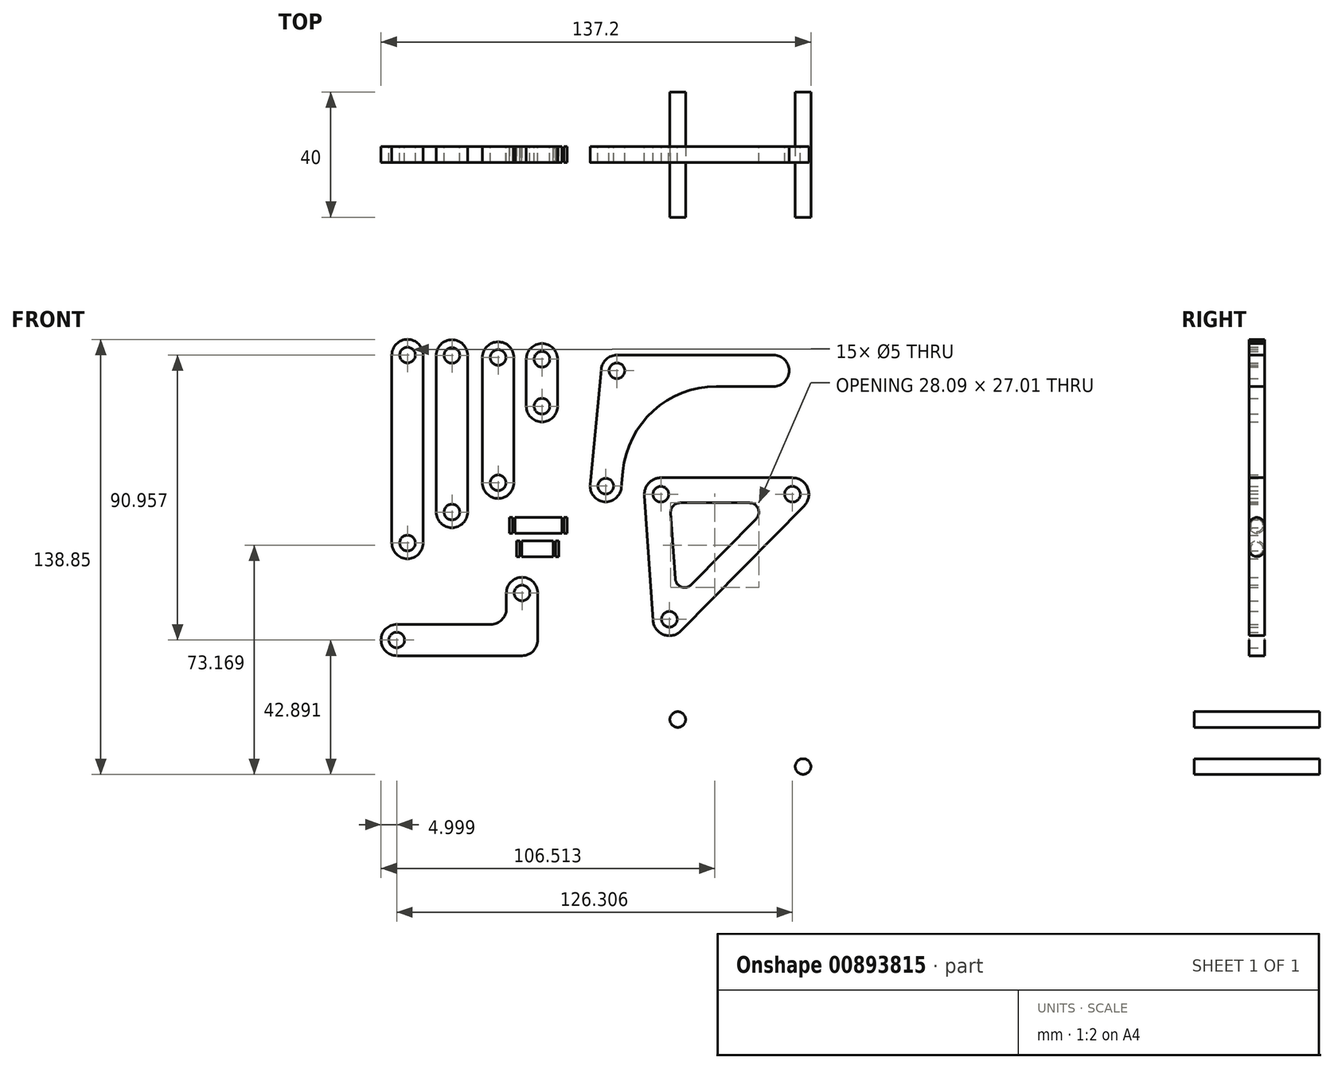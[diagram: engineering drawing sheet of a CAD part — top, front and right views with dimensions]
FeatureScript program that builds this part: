
annotation { "Feature Type Name" : "Feature", "Feature Type Description" : "" }
export const myFeature = defineFeature(function(context is Context, id is Id, definition is map)
    precondition{}
    {
        {
            assignVariable(context, id + "F0", {"name" : "T", "anyValue" : 5});
        }
        {
            assignVariable(context, id + "F1", {"name" : "W", "anyValue" : 40});
        }
        {
            var Q0;
            Q0=qCreatedBy(makeId("Front.planeOp"),FACE);
            var sketch = newSketch(context, id + "F2", { "sketchPlane" : qUnion([Q0])});
            skLineSegment(sketch, "E0", {"start": v(-8.35, 51.22) * mm, "end": v(-8.35, 66.22) * mm});
            skLineSegment(sketch, "E1", {"start": v(-18.35, 51.22) * mm, "end": v(-18.35, 66.22) * mm});
            skArc(sketch, "E2", {"start": v(-8.35, 66.22) * mm, "mid": v(-13.35, 71.22) * mm, "end": v(-18.35, 66.22) * mm});
            skArc(sketch, "E3", {"start": v(-18.35, 51.22) * mm, "mid": v(-13.35, 46.22) * mm, "end": v(-8.35, 51.22) * mm});
            skCircle(sketch, "E4", {"center": v(-13.35, 66.22) * mm, "radius": 2.5 * mm});
            skCircle(sketch, "E5", {"center": v(-13.35, 51.22) * mm, "radius": 2.5 * mm});
            skSolve(sketch);
        }
        {
            var Q0;
            Q0=qSketchRegion(id+"F2",true);
            extrude(context, id + "F3", {"entities" : qUnion([Q0]), "depth" : (getVariable(context, 'T')) * mm, "offsetDistance" : 25 * mm, "symmetric" : true});
        }
        {
            var Q0;
            Q0=qCreatedBy(makeId("Front.planeOp"),FACE);
            var sketch = newSketch(context, id + "F4", { "sketchPlane" : qUnion([Q0])});
            skLineSegment(sketch, "E6", {"start": v(-32.34, 66.78) * mm, "end": v(-32.34, 26.78) * mm});
            skLineSegment(sketch, "E7", {"start": v(-22.34, 26.78) * mm, "end": v(-22.34, 66.78) * mm});
            skArc(sketch, "E8", {"start": v(-22.34, 66.78) * mm, "mid": v(-27.34, 71.78) * mm, "end": v(-32.34, 66.78) * mm});
            skArc(sketch, "E9", {"start": v(-32.34, 26.78) * mm, "mid": v(-27.34, 21.78) * mm, "end": v(-22.34, 26.78) * mm});
            skCircle(sketch, "E10", {"center": v(-27.34, 26.78) * mm, "radius": 2.5 * mm});
            skCircle(sketch, "E11", {"center": v(-27.34, 66.78) * mm, "radius": 2.5 * mm});
            skSolve(sketch);
        }
        {
            var Q0;
            Q0=qSketchRegion(id+"F4",true);
            extrude(context, id + "F5", {"entities" : qUnion([Q0]), "depth" : (getVariable(context, 'T')) * mm, "offsetDistance" : 25 * mm, "symmetric" : true});
        }
        {
            var Q0;
            Q0=qCreatedBy(makeId("Front.planeOp"),FACE);
            var sketch = newSketch(context, id + "F6", { "sketchPlane" : qUnion([Q0])});
            skLineSegment(sketch, "E12", {"start": v(-47.08, 67.45) * mm, "end": v(-47.08, 17.45) * mm});
            skLineSegment(sketch, "E13", {"start": v(-37.08, 67.45) * mm, "end": v(-37.08, 17.45) * mm});
            skArc(sketch, "E14", {"start": v(-47.08, 17.45) * mm, "mid": v(-42.08, 12.45) * mm, "end": v(-37.08, 17.45) * mm});
            skArc(sketch, "E15", {"start": v(-37.08, 67.45) * mm, "mid": v(-42.08, 72.45) * mm, "end": v(-47.08, 67.45) * mm});
            skCircle(sketch, "E16", {"center": v(-42.08, 67.45) * mm, "radius": 2.5 * mm});
            skCircle(sketch, "E17", {"center": v(-42.08, 17.45) * mm, "radius": 2.5 * mm});
            skSolve(sketch);
        }
        {
            var Q0;
            Q0=qSketchRegion(id+"F6",true);
            extrude(context, id + "F7", {"entities" : qUnion([Q0]), "depth" : (getVariable(context, 'T')) * mm, "offsetDistance" : 25 * mm, "symmetric" : true});
        }
        {
            var Q0;
            Q0=qCreatedBy(makeId("Front.planeOp"),FACE);
            var sketch = newSketch(context, id + "F8", { "sketchPlane" : qUnion([Q0])});
            skLineSegment(sketch, "E18", {"start": v(-61.26, 67.56) * mm, "end": v(-61.26, 7.56) * mm});
            skLineSegment(sketch, "E19", {"start": v(-51.26, 7.56) * mm, "end": v(-51.26, 67.56) * mm});
            skArc(sketch, "E20", {"start": v(-51.26, 67.56) * mm, "mid": v(-56.26, 72.56) * mm, "end": v(-61.26, 67.56) * mm});
            skArc(sketch, "E21", {"start": v(-61.26, 7.56) * mm, "mid": v(-56.26, 2.56) * mm, "end": v(-51.26, 7.56) * mm});
            skCircle(sketch, "E22", {"center": v(-56.26, 67.56) * mm, "radius": 2.5 * mm});
            skCircle(sketch, "E23", {"center": v(-56.26, 7.56) * mm, "radius": 2.5 * mm});
            skSolve(sketch);
        }
        {
            var Q0;
            Q0=qSketchRegion(id+"F8",true);
            extrude(context, id + "F9", {"entities" : qUnion([Q0]), "depth" : (getVariable(context, 'T')) * mm, "offsetDistance" : 25 * mm, "symmetric" : true});
        }
        {
            var Q0;
            Q0=qCreatedBy(makeId("Front.planeOp"),FACE);
            var sketch = newSketch(context, id + "F10", { "sketchPlane" : qUnion([Q0])});
            skLineSegment(sketch, "E24", {"start": v(60.57, 67.55) * mm, "end": v(10.57, 67.55) * mm});
            skLineSegment(sketch, "E25", {"start": v(5.6, 63.03) * mm, "end": v(2.04, 26.2) * mm});
            skLineSegment(sketch, "E26", {"start": v(12, 25.24) * mm, "end": v(12.5, 30.44) * mm});
            skLineSegment(sketch, "E27", {"start": v(42.35, 57.55) * mm, "end": v(60.57, 57.55) * mm});
            skArc(sketch, "E28", {"start": v(2.04, 26.2) * mm, "mid": v(6.53, 20.74) * mm, "end": v(12, 25.24) * mm});
            skArc(sketch, "E29", {"start": v(10.57, 67.55) * mm, "mid": v(7.21, 66.25) * mm, "end": v(5.6, 63.03) * mm});
            skArc(sketch, "E30", {"start": v(60.57, 57.55) * mm, "mid": v(65.57, 62.55) * mm, "end": v(60.57, 67.55) * mm});
            skArc(sketch, "E31", {"start": v(42.35, 57.55) * mm, "mid": v(22.19, 49.76) * mm, "end": v(12.5, 30.44) * mm});
            skCircle(sketch, "E32", {"center": v(7.01, 25.72) * mm, "radius": 2.5 * mm});
            skCircle(sketch, "E33", {"center": v(10.57, 62.55) * mm, "radius": 2.5 * mm});
            skSolve(sketch);
        }
        {
            var Q0;
            Q0=makeQuery(id+"F10.imprint","IMPRINT",FACE,{"disambiguationData":[TD([[makeQuery(id+"F10.imprint","IMPRINT",EDGE,{"derivedFrom":sQuery(id+"F10.wireOp",EDGE,"E24")}),1.0]])]});
            extrude(context, id + "F11", {"entities" : qUnion([Q0]), "depth" : (getVariable(context, 'T')) * mm, "offsetDistance" : 25 * mm, "symmetric" : true});
        }
        {
            var Q0;
            Q0=qCreatedBy(makeId("Front.planeOp"),FACE);
            var sketch = newSketch(context, id + "F12", { "sketchPlane" : qUnion([Q0])});
            skLineSegment(sketch, "E34", {"start": v(19.37, 22.78) * mm, "end": v(22.08, -17.13) * mm});
            skLineSegment(sketch, "E35", {"start": v(31.06, -20.46) * mm, "end": v(70.35, 19.45) * mm});
            skLineSegment(sketch, "E36", {"start": v(66.6, 28.38) * mm, "end": v(24.6, 28.38) * mm});
            skArc(sketch, "E37", {"start": v(24.6, 28.38) * mm, "mid": v(20.77, 26.72) * mm, "end": v(19.37, 22.78) * mm});
            skArc(sketch, "E38", {"start": v(22.08, -17.13) * mm, "mid": v(25.5, -21.7) * mm, "end": v(31.06, -20.46) * mm});
            skArc(sketch, "E39", {"start": v(70.35, 19.45) * mm, "mid": v(71.45, 25.16) * mm, "end": v(66.6, 28.38) * mm});
            skCircle(sketch, "E40", {"center": v(24.6, 23.13) * mm, "radius": 2.5 * mm});
            skCircle(sketch, "E41", {"center": v(27.32, -16.77) * mm, "radius": 2.5 * mm});
            skCircle(sketch, "E42", {"center": v(66.6, 23.13) * mm, "radius": 2.5 * mm});
            skLineSegment(sketch, "E43", {"start": v(30.76, 20.38) * mm, "end": v(52.88, 20.38) * mm});
            skLineSegment(sketch, "E44", {"start": v(55.01, 15.28) * mm, "end": v(34.33, -5.74) * mm});
            skLineSegment(sketch, "E45", {"start": v(27.77, 17.18) * mm, "end": v(29.2, -3.83) * mm});
            skArc(sketch, "E46", {"start": v(29.2, -3.83) * mm, "mid": v(31.15, -6.44) * mm, "end": v(34.33, -5.74) * mm});
            skArc(sketch, "E47", {"start": v(30.76, 20.38) * mm, "mid": v(28.57, 19.43) * mm, "end": v(27.77, 17.18) * mm});
            skArc(sketch, "E48", {"start": v(55.01, 15.28) * mm, "mid": v(55.64, 18.54) * mm, "end": v(52.88, 20.38) * mm});
            skLineSegment(sketch, "E49", {"start": v(52.88, 28.38) * mm, "end": v(52.88, 20.38) * mm, "construction": true});
            skLineSegment(sketch, "E50", {"start": v(60.71, 9.67) * mm, "end": v(55.01, 15.28) * mm, "construction": true});
            skLineSegment(sketch, "E51", {"start": v(19.78, 16.64) * mm, "end": v(27.77, 17.18) * mm, "construction": true});
            skSolve(sketch);
        }
        {
            var Q0;
            Q0=qSketchRegion(id+"F12",true);
            extrude(context, id + "F13", {"entities" : qUnion([Q0]), "depth" : (getVariable(context, 'T')) * mm, "offsetDistance" : 25 * mm, "symmetric" : true});
        }
        {
            var Q0;
            Q0=qCreatedBy(makeId("Front.planeOp"),FACE);
            var sketch = newSketch(context, id + "F14", { "sketchPlane" : qUnion([Q0])});
            skLineSegment(sketch, "E52", {"start": v(-21.44, 5.72) * mm, "end": v(-21.44, 8.22) * mm});
            skLineSegment(sketch, "E53", {"start": v(-21.44, 8.22) * mm, "end": v(-20.44, 8.22) * mm});
            skLineSegment(sketch, "E54", {"start": v(-20.44, 8.22) * mm, "end": v(-20.44, 7.72) * mm});
            skLineSegment(sketch, "E55", {"start": v(-20.44, 7.72) * mm, "end": v(-19.74, 7.72) * mm});
            skLineSegment(sketch, "E56", {"start": v(-19.74, 7.72) * mm, "end": v(-19.74, 8.22) * mm});
            skLineSegment(sketch, "E57", {"start": v(-19.74, 8.22) * mm, "end": v(-9.74, 8.22) * mm});
            skLineSegment(sketch, "E58", {"start": v(-9.74, 8.22) * mm, "end": v(-9.74, 7.72) * mm});
            skLineSegment(sketch, "E59", {"start": v(-9.74, 7.72) * mm, "end": v(-9.04, 7.72) * mm});
            skLineSegment(sketch, "E60", {"start": v(-9.04, 7.72) * mm, "end": v(-9.04, 8.22) * mm});
            skLineSegment(sketch, "E61", {"start": v(-9.04, 8.22) * mm, "end": v(-8.04, 8.22) * mm});
            skLineSegment(sketch, "E62", {"start": v(-8.04, 8.22) * mm, "end": v(-8.04, 5.72) * mm});
            skLineSegment(sketch, "E63", {"start": v(-8.04, 5.72) * mm, "end": v(-21.44, 5.72) * mm});
            skSolve(sketch);
        }
        {
            var Q0;
            Q0=makeQuery(id+"F14.imprint","IMPRINT",FACE,{"disambiguationData":[TD([[makeQuery(id+"F14.imprint","IMPRINT",EDGE,{"derivedFrom":sQuery(id+"F14.wireOp",EDGE,"E52")}),-1.0]])]});
            var Q1;
            Q1=sQuery(id+"F14.wireOp",EDGE,"E63");
            revolve(context, id + "F15", {"surfaceOperationType" : NewSurfaceOperationType.NEW, "entities" : qUnion([Q0]), "axis" : qUnion([Q1]), "revolveType" : RevolveType.FULL});
        }
        {
            var Q0;
            Q0=qCreatedBy(makeId("Front.planeOp"),FACE);
            var sketch = newSketch(context, id + "F16", { "sketchPlane" : qUnion([Q0])});
            skLineSegment(sketch, "E64", {"start": v(-23.7, 15.7) * mm, "end": v(-23.7, 13.2) * mm});
            skLineSegment(sketch, "E65", {"start": v(-23.7, 13.2) * mm, "end": v(-5.3, 13.2) * mm});
            skLineSegment(sketch, "E66", {"start": v(-5.3, 13.2) * mm, "end": v(-5.3, 15.7) * mm});
            skLineSegment(sketch, "E67", {"start": v(-5.3, 15.7) * mm, "end": v(-6.3, 15.7) * mm});
            skLineSegment(sketch, "E68", {"start": v(-6.3, 15.7) * mm, "end": v(-6.3, 15.2) * mm});
            skLineSegment(sketch, "E69", {"start": v(-6.3, 15.2) * mm, "end": v(-7, 15.2) * mm});
            skLineSegment(sketch, "E70", {"start": v(-7, 15.2) * mm, "end": v(-7, 15.7) * mm});
            skLineSegment(sketch, "E71", {"start": v(-7, 15.7) * mm, "end": v(-22, 15.7) * mm});
            skLineSegment(sketch, "E72", {"start": v(-22, 15.7) * mm, "end": v(-22, 15.2) * mm});
            skLineSegment(sketch, "E73", {"start": v(-22, 15.2) * mm, "end": v(-22.7, 15.2) * mm});
            skLineSegment(sketch, "E74", {"start": v(-22.7, 15.2) * mm, "end": v(-22.7, 15.7) * mm});
            skLineSegment(sketch, "E75", {"start": v(-22.7, 15.7) * mm, "end": v(-23.7, 15.7) * mm});
            skSolve(sketch);
        }
        {
            var Q0;
            Q0=qSketchRegion(id+"F16",true);
            var Q1;
            Q1=sQuery(id+"F16.wireOp",EDGE,"E65");
            revolve(context, id + "F17", {"surfaceOperationType" : NewSurfaceOperationType.NEW, "entities" : qUnion([Q0]), "axis" : qUnion([Q1]), "revolveType" : RevolveType.FULL});
        }
        {
            var Q0;
            Q0=qCreatedBy(makeId("Front.planeOp"),FACE);
            var sketch = newSketch(context, id + "F18", { "sketchPlane" : qUnion([Q0])});
            skLineSegment(sketch, "E76", {"start": v(-59.7, -18.4) * mm, "end": v(-29.7, -18.4) * mm});
            skLineSegment(sketch, "E77", {"start": v(-24.7, -13.4) * mm, "end": v(-24.7, -8.4) * mm});
            skLineSegment(sketch, "E78", {"start": v(-14.7, -8.4) * mm, "end": v(-14.7, -23.4) * mm});
            skLineSegment(sketch, "E79", {"start": v(-19.7, -28.4) * mm, "end": v(-59.7, -28.4) * mm});
            skArc(sketch, "E80", {"start": v(-59.7, -18.4) * mm, "mid": v(-64.7, -23.4) * mm, "end": v(-59.7, -28.4) * mm});
            skArc(sketch, "E81", {"start": v(-14.7, -8.4) * mm, "mid": v(-19.7, -3.4) * mm, "end": v(-24.7, -8.4) * mm});
            skPoint(sketch, "E82.visualSharp", {"position": v(-24.7, -18.4) * mm});
            skArc(sketch, "E82.filletArc", {"start": v(-29.7, -18.4) * mm, "mid": v(-26.17, -16.93) * mm, "end": v(-24.7, -13.4) * mm});
            skPoint(sketch, "E83.visualSharp", {"position": v(-14.7, -28.4) * mm});
            skArc(sketch, "E83.filletArc", {"start": v(-19.7, -28.4) * mm, "mid": v(-16.17, -26.93) * mm, "end": v(-14.7, -23.4) * mm});
            skCircle(sketch, "E84", {"center": v(-59.7, -23.4) * mm, "radius": 2.5 * mm});
            skCircle(sketch, "E85", {"center": v(-19.7, -8.4) * mm, "radius": 2.5 * mm});
            skSolve(sketch);
        }
        {
            var Q0;
            Q0=qSketchRegion(id+"F18",true);
            extrude(context, id + "F19", {"entities" : qUnion([Q0]), "depth" : (getVariable(context, 'T')) * mm, "offsetDistance" : 25 * mm, "symmetric" : true});
        }
        {
            var Q0;
            Q0=qCreatedBy(makeId("Front.planeOp"),FACE);
            var sketch = newSketch(context, id + "F20", { "sketchPlane" : qUnion([Q0])});
            skLineSegment(sketch, "E86.bottom", {"start": v(-80, -39.79) * mm, "end": v(120, -39.79) * mm});
            skLineSegment(sketch, "E86.top", {"start": v(-80, -69.79) * mm, "end": v(120, -69.79) * mm});
            skLineSegment(sketch, "E86.left", {"start": v(-80, -39.79) * mm, "end": v(-80, -69.79) * mm});
            skLineSegment(sketch, "E86.right", {"start": v(120, -39.79) * mm, "end": v(120, -69.79) * mm});
            skSolve(sketch);
        }
        {
            var Q0;
            Q0=makeQuery(id+"F20.imprint","IMPRINT",FACE,{"disambiguationData":[TD([[makeQuery(id+"F20.imprint","IMPRINT",EDGE,{"derivedFrom":sQuery(id+"F20.wireOp",EDGE,"E86.bottom")}),-1.0]])]});
            extrude(context, id + "F21", {"entities" : qUnion([Q0]), "depth" : (getVariable(context, 'W')) * mm, "offsetDistance" : 25 * mm, "symmetric" : true});
        }
        {
            var Q0;
            Q0=makeQuery(id+"F21.opExtrude","CAP_FACE",FACE,{"disambiguationData":[OSD([sQuery(id+"F20.wireOp",EDGE,"E86.bottom"),sQuery(id+"F20.wireOp",EDGE,"E86.top"),sQuery(id+"F20.wireOp",EDGE,"E86.left"),sQuery(id+"F20.wireOp",EDGE,"E86.right")])],"isStart":false});
            var sketch = newSketch(context, id + "F22", { "sketchPlane" : qUnion([Q0])});
            skCircle(sketch, "E87", {"center": v(-70, -63.79) * mm, "radius": 2.5 * mm});
            skCircle(sketch, "E88", {"center": v(-30, -48.79) * mm, "radius": 2.5 * mm});
            skLineSegment(sketch, "E89", {"start": v(-70, -63.79) * mm, "end": v(-30, -63.79) * mm, "construction": true});
            skLineSegment(sketch, "E90", {"start": v(-30, -63.79) * mm, "end": v(-30, -48.79) * mm, "construction": true});
            skCircle(sketch, "E91.MirrorC", {"center": v(30, -48.79) * mm, "radius": 2.5 * mm});
            skCircle(sketch, "E92.MirrorC", {"center": v(70, -63.79) * mm, "radius": 2.5 * mm});
            skSolve(sketch);
        }
        {
            var Q0;
            Q0=makeQuery(id+"F22.imprint","IMPRINT",FACE,{"disambiguationData":[TD([[makeQuery(id+"F22.imprint","IMPRINT",EDGE,{"derivedFrom":sQuery(id+"F22.wireOp",EDGE,"E87")}),1.0]])]});
            var Q1;
            Q1=makeQuery(id+"F22.imprint","IMPRINT",FACE,{"disambiguationData":[TD([[makeQuery(id+"F22.imprint","IMPRINT",EDGE,{"derivedFrom":sQuery(id+"F22.wireOp",EDGE,"E88")}),1.0]])]});
            var Q2;
            Q2=makeQuery(id+"F22.imprint","IMPRINT",FACE,{"disambiguationData":[TD([[makeQuery(id+"F22.imprint","IMPRINT",EDGE,{"derivedFrom":sQuery(id+"F22.wireOp",EDGE,"E91.MirrorC")}),-1.0]])]});
            var Q3;
            Q3=makeQuery(id+"F22.imprint","IMPRINT",FACE,{"disambiguationData":[TD([[makeQuery(id+"F22.imprint","IMPRINT",EDGE,{"derivedFrom":sQuery(id+"F22.wireOp",EDGE,"E92.MirrorC")}),-1.0]])]});
            var Q4;
            Q4=makeQuery(id+"F21.opExtrude","CAP_FACE",FACE,{"disambiguationData":[OSD([sQuery(id+"F20.wireOp",EDGE,"E86.bottom"),sQuery(id+"F20.wireOp",EDGE,"E86.top"),sQuery(id+"F20.wireOp",EDGE,"E86.left"),sQuery(id+"F20.wireOp",EDGE,"E86.right")])],"isStart":true});
            extrude(context, id + "F23", {"entities" : qUnion([Q0, Q1, Q2, Q3]), "operationType" : NewBodyOperationType.REMOVE, "endBound" : BoundingType.UP_TO_SURFACE, "oppositeDirection" : true, "depth" : 25 * mm, "endBoundEntityFace" : qUnion([Q4]), "offsetDistance" : 25 * mm});
        }
    });
